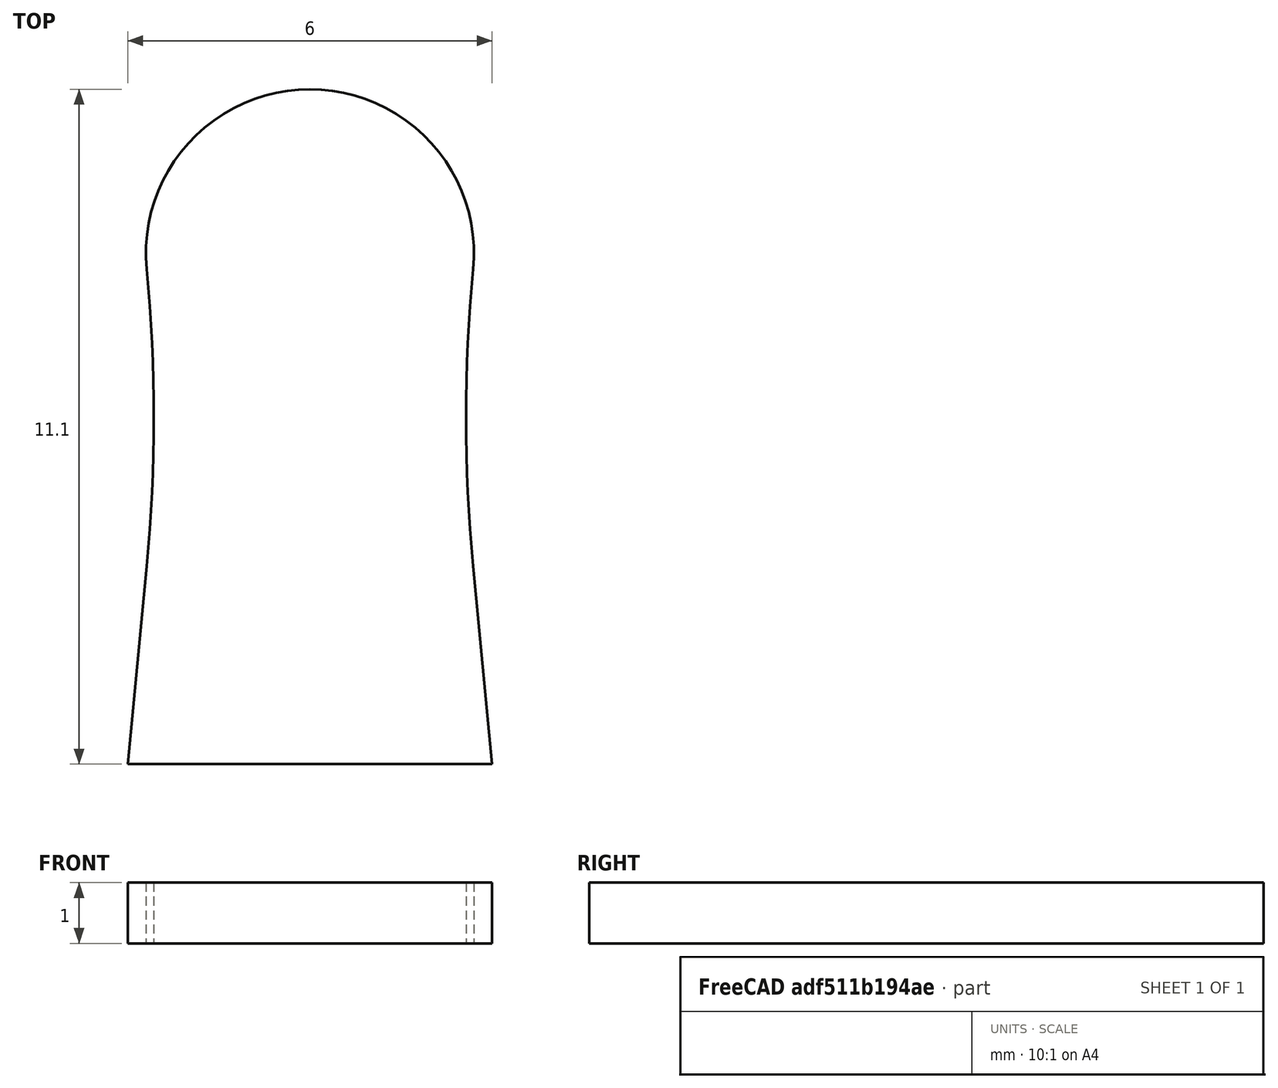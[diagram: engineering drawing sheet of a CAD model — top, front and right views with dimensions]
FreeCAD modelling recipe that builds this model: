
FCSTD DOCUMENT  (FreeCAD 0.18.1R)
Label: PCB_Telemetre_Frontal
License: All rights reserved
LicenseURL: http://en.wikipedia.org/wiki/All_rights_reserved
objects: Sketcher::SketchObject×1, PartDesign::Pad×1, PartDesign::Body×1
note: 4 computed .brp shape members not serialized (recipe doc carries the construction recipe); baked Part::Feature solids carry a one-line shape summary decoded from their .brp

FEATURE [Sketcher::SketchObject] Sketch
  MapMode = 5
  Support = -> [XY_Plane]
  sketch-geometry (8):
    g0: LineSegment StartX=3 StartY=0 StartZ=0 EndX=-3 EndY=0 EndZ=0
    g1: Circle [constr] CenterX=0 CenterY=8.4 CenterZ=0 NormalX=0 NormalY=0 NormalZ=1 AngleXU=0 Radius=2.7
    g2: Circle [constr] CenterX=0 CenterY=3 CenterZ=0 NormalX=0 NormalY=0 NormalZ=1 AngleXU=0 Radius=2.7
    g3: ArcOfCircle CenterX=0 CenterY=8.4 CenterZ=0 NormalX=0 NormalY=0 NormalZ=1 AngleXU=0 Radius=2.7 StartAngle=6.1876 EndAngle=9.52036
    g4: ArcOfCircle CenterX=-28.1622 CenterY=5.7 CenterZ=0 NormalX=0 NormalY=0 NormalZ=1 AngleXU=0 Radius=25.5913 StartAngle=6.1876 EndAngle=6.37877
    g5: LineSegment StartX=-3 StartY=0 StartZ=0 EndX=-2.68768 EndY=3.25768 EndZ=0
    g6: ArcOfCircle CenterX=28.1622 CenterY=5.7 CenterZ=0 NormalX=0 NormalY=0 NormalZ=1 AngleXU=0 Radius=25.5913 StartAngle=3.04601 EndAngle=3.23717
    g7: LineSegment StartX=3 StartY=0 StartZ=0 EndX=2.68768 EndY=3.25768 EndZ=0
  constraints (21):
    c: PointOnObject(g0,g-1)
    c: Radius(g2) = 2.7
    c: Distance(g2,g0) = 3
    c: Tangent(g1,g2)
    c: PointOnObject(g2,g-2)
    c: Coincident(g3,g1)
    c: PointOnObject(g4,g2)
    c: Coincident(g5,g0)
    c: Tangent(g4,g3) = 1.5708
    c: DistanceX(g0,g0) = 6
    c: Symmetric(g0,g0,g-2)
    c: Coincident(g7,g0)
    c: Tangent(g7,g6) = 1.5708
    c: Tangent(g7,g2)
    c: Tangent(g5,g2)
    c: PointOnObject(g3,g-2)
    c: Equal(g1,g2)
    c: Tangent(g4,g5) = -1.5708
    c: PointOnObject(g6,g2)
    c: Tangent(g6,g3) = 1.5708
    c: PointOnObject(g3,g1)
FEATURE [PartDesign::Pad] Pad
  Length = 1
  Length2 = 100
  Profile = -> Sketch
  Type = 0
FEATURE [PartDesign::Body] Body
  Group = -> [Sketch,Pad]
  Origin = -> Origin
  Tip = -> Pad
